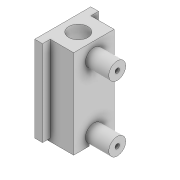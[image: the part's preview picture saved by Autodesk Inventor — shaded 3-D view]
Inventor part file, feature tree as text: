
AUTODESK INVENTOR PART (.ipt)
format: ipt  version: 2022 (Build 260153000, 153)  size: 174,592 bytes
history: native  units: mm
features: extrude x6, sketch x6, projected_geometry x1
ambient origin geometry x8: Origin, YZ Plane, XZ Plane, XY Plane, X Axis, Y Axis, Z Axis, Center Point
bodies: Solid1 (feature_tree)
feature tree (13):
  extrude  "Extrusion1"  Depth=10.0mm
  extrude  "Extrusion2"  Depth=10.0mm
  sketch  "Sketch3"  dims[d4=13.0mm d5=55.0mm d6=0.0mm]
  extrude  "Extrusion3"  Depth=55.0mm TaperAngle=0.0deg
  extrude  "Extrusion6"  Depth=4.0mm
  extrude  "Extrusion7"  Depth=46.0mm
  extrude  "Extrusion8"  Depth=2.0mm
  sketch  "Sketch1"  dims[d0=12.3mm d1=10.0mm]
  sketch  "Sketch2"  dims[d2=10.0mm d3=13.0mm]
  projected_geometry  "Projected Loop1"
  sketch  "Sketch6"  dims[d7=2.9mm d8=4.0mm]
  sketch  "Sketch7"  dims[d9=2.9mm d10=46.0mm]
  sketch  "Sketch8"  dims[d11=13.0mm d12=13.0mm d13=55.0mm d14=0.0mm d15=4.0mm d16=4.0mm d17=15.0mm d18=0.0mm d19=3.2mm d20=3.2mm d21=3.2mm d22=3.2mm d23=4.0mm d24=4.0mm d25=4.0mm d26=4.0mm d31=5.0mm d32=5.0mm d33=0.0mm d34=5.0mm d35=5.0mm d36=0.0mm d37=10.0mm d38=10.0mm d39=2.0mm d40=0.0mm]
